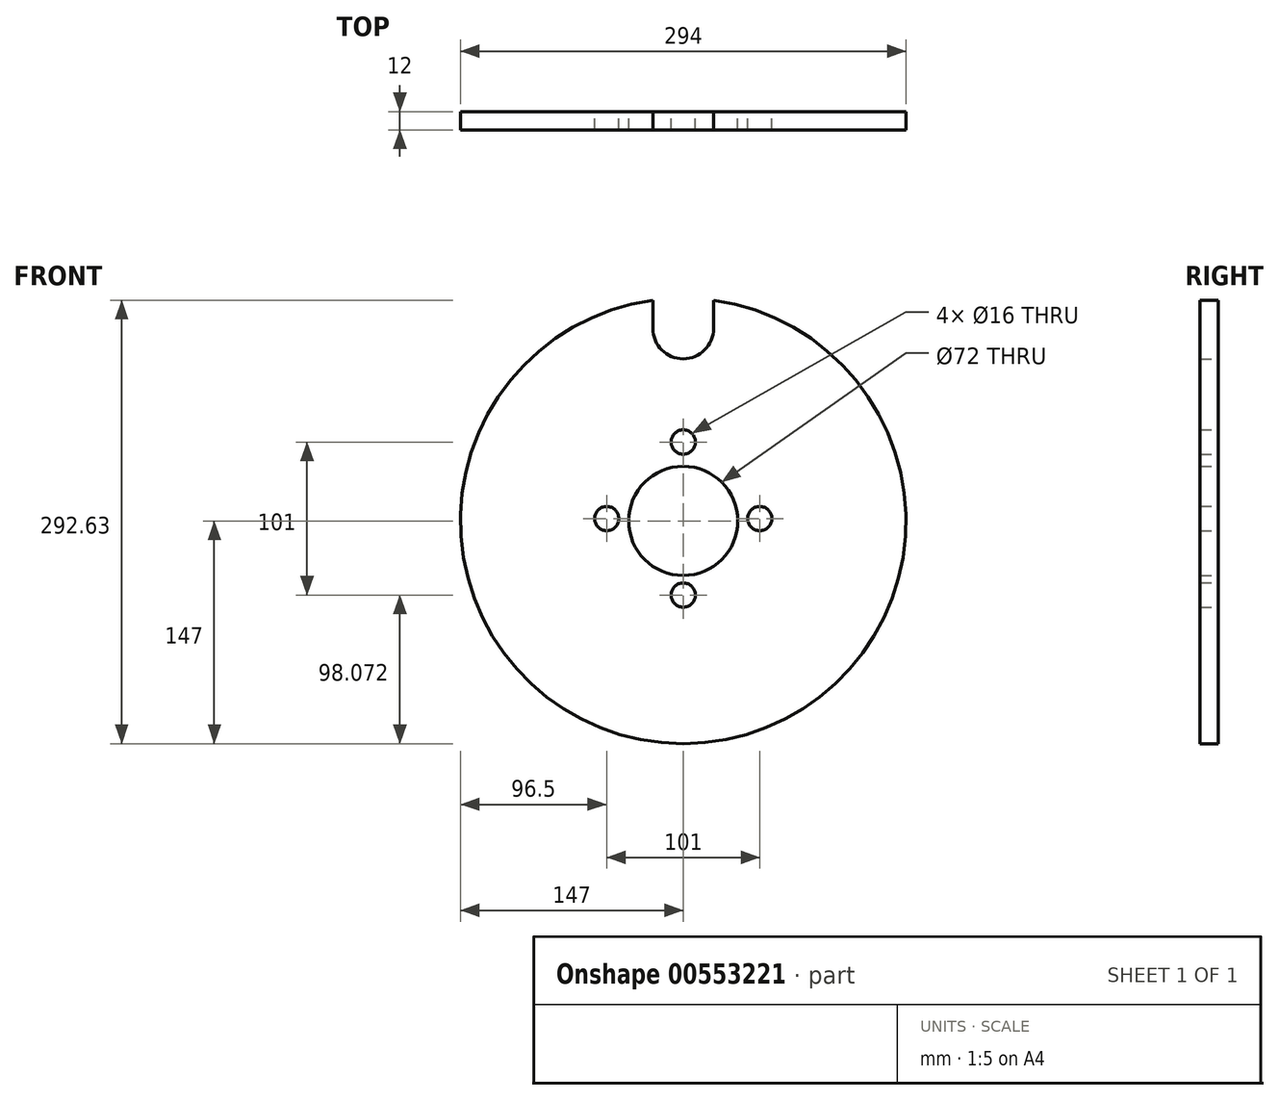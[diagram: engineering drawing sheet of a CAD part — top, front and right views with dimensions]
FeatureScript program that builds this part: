
annotation { "Feature Type Name" : "Feature", "Feature Type Description" : "" }
export const myFeature = defineFeature(function(context is Context, id is Id, definition is map)
    precondition{}
    {
        {
            var Q0;
            Q0=qCreatedBy(makeId("Front.planeOp"),FACE);
            var sketch = newSketch(context, id + "F0", { "sketchPlane" : qUnion([Q0])});
            skArc(sketch, "E0", {"start": v(-20, 145.63) * mm, "mid": v(0, -147) * mm, "end": v(20, 145.63) * mm});
            skCircle(sketch, "E1", {"center": v(0, 0) * mm, "radius": 36 * mm});
            skCircle(sketch, "E2", {"center": v(0, 52.07) * mm, "radius": 8 * mm});
            skCircle(sketch, "E3.1.0", {"center": v(-50.5, 1.57) * mm, "radius": 8 * mm});
            skCircle(sketch, "E3.2.0", {"center": v(0, -48.93) * mm, "radius": 8 * mm});
            skCircle(sketch, "E3.3.0", {"center": v(50.5, 1.57) * mm, "radius": 8 * mm});
            skPoint(sketch, "E3.center", {"position": v(0, 1.57) * mm});
            skLineSegment(sketch, "E4", {"start": v(-20, 127) * mm, "end": v(-20, 145.63) * mm});
            skLineSegment(sketch, "E5", {"start": v(20, 127) * mm, "end": v(20, 145.63) * mm});
            skArc(sketch, "E6", {"start": v(-20, 127) * mm, "mid": v(0, 107) * mm, "end": v(20, 127) * mm});
            skSolve(sketch);
        }
        {
            var Q0;
            Q0=makeQuery(id+"F0.imprint","IMPRINT",FACE,{"disambiguationData":[TD([[makeQuery(id+"F0.imprint","IMPRINT",EDGE,{"derivedFrom":sQuery(id+"F0.wireOp",EDGE,"E0")}),1.0]])]});
            extrude(context, id + "F1", {"entities" : qUnion([Q0]), "depth" : 12 * mm, "offsetDistance" : 25 * mm});
        }
    });
